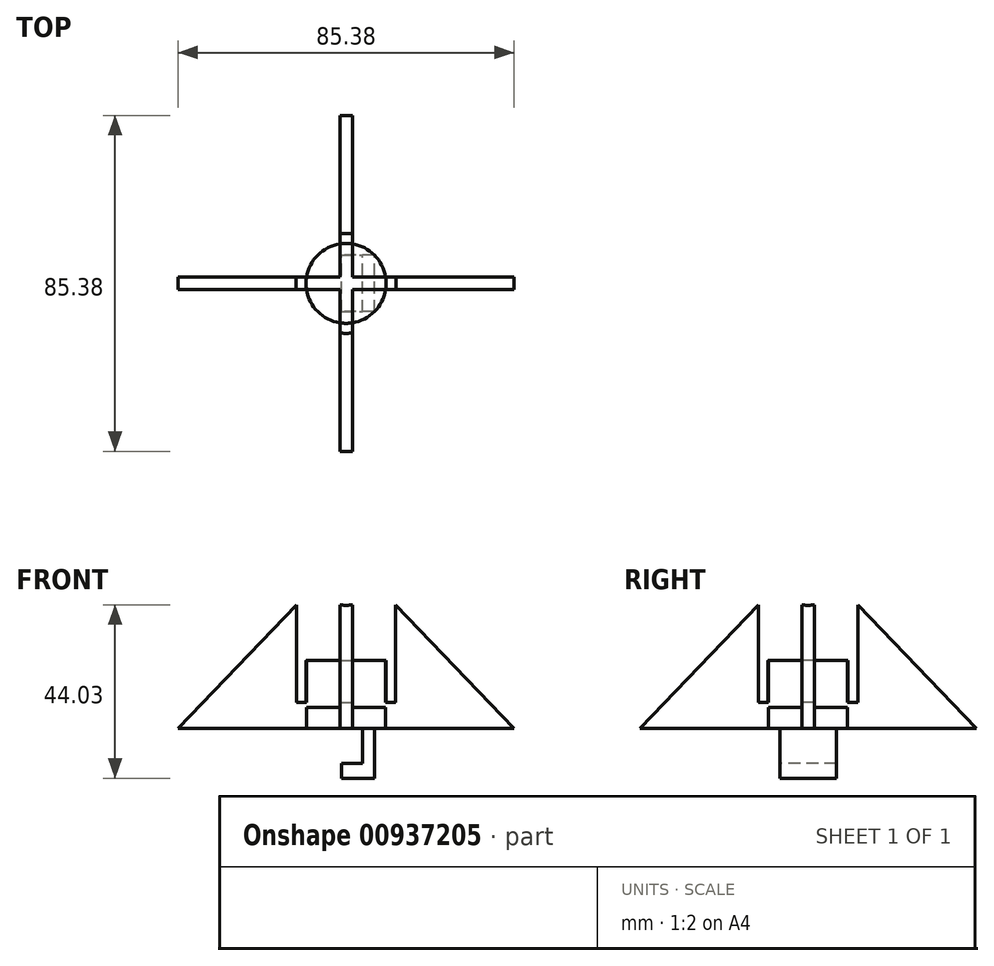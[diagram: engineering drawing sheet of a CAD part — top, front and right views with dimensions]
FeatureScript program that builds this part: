
annotation { "Feature Type Name" : "Feature", "Feature Type Description" : "" }
export const myFeature = defineFeature(function(context is Context, id is Id, definition is map)
    precondition{}
    {
        {
            var Q0;
            Q0=qCreatedBy(makeId("Top.planeOp"),FACE);
            var sketch = newSketch(context, id + "F0", { "sketchPlane" : qUnion([Q0])});
            skPoint(sketch, "E0", {"position": v(-50.8, 50.8) * mm});
            skLineSegment(sketch, "E1.bottom", {"start": v(-50.8, 50.8) * mm, "end": v(50.8, 50.8) * mm});
            skLineSegment(sketch, "E1.top", {"start": v(-50.8, -50.8) * mm, "end": v(50.8, -50.8) * mm});
            skLineSegment(sketch, "E1.left", {"start": v(-50.8, 50.8) * mm, "end": v(-50.8, -50.8) * mm});
            skLineSegment(sketch, "E1.right", {"start": v(50.8, 50.8) * mm, "end": v(50.8, -50.8) * mm});
            skPoint(sketch, "E1.middle", {"position": v(0, 0) * mm});
            skSolve(sketch);
        }
        {
            var Q0;
            Q0=makeQuery(id+"F0.imprint","IMPRINT",FACE,{"disambiguationData":[TD([[makeQuery(id+"F0.imprint","IMPRINT",EDGE,{"derivedFrom":sQuery(id+"F0.wireOp",EDGE,"E1.bottom")}),-1.0]])]});
            extrude(context, id + "F1", {"entities" : qUnion([Q0]), "depth" : 50.8 * mm, "offsetDistance" : 25.4 * mm});
        }
        {
            var Q0;
            Q0=makeQuery(id+"F1.opExtrude","CAP_FACE",FACE,{"disambiguationData":[OSD([sQuery(id+"F0.wireOp",EDGE,"E1.bottom"),sQuery(id+"F0.wireOp",EDGE,"E1.top"),sQuery(id+"F0.wireOp",EDGE,"E1.left"),sQuery(id+"F0.wireOp",EDGE,"E1.right")])],"isStart":false});
            var sketch = newSketch(context, id + "F2", { "sketchPlane" : qUnion([Q0])});
            skPoint(sketch, "E2.middle", {"position": v(0, 0) * mm});
            skLineSegment(sketch, "E3.bottom", {"start": v(-50.8, 50.8) * mm, "end": v(-1.59, 50.8) * mm});
            skLineSegment(sketch, "E3.top", {"start": v(-42.69, 1.59) * mm, "end": v(-1.59, 1.59) * mm});
            skLineSegment(sketch, "E3.left", {"start": v(-50.8, 50.8) * mm, "end": v(-50.8, 1.59) * mm});
            skLineSegment(sketch, "E3.right", {"start": v(-1.59, 42.69) * mm, "end": v(-1.59, 1.59) * mm});
            skLineSegment(sketch, "E4.bottom", {"start": v(1.59, 1.59) * mm, "end": v(42.69, 1.59) * mm});
            skLineSegment(sketch, "E4.top", {"start": v(1.59, 50.8) * mm, "end": v(50.8, 50.8) * mm});
            skLineSegment(sketch, "E4.left", {"start": v(1.59, 1.59) * mm, "end": v(1.59, 42.69) * mm});
            skLineSegment(sketch, "E4.right", {"start": v(50.8, 1.59) * mm, "end": v(50.8, 50.8) * mm});
            skLineSegment(sketch, "E5.bottom", {"start": v(1.59, -1.59) * mm, "end": v(42.69, -1.59) * mm});
            skLineSegment(sketch, "E5.top", {"start": v(1.59, -50.8) * mm, "end": v(50.8, -50.8) * mm});
            skLineSegment(sketch, "E5.left", {"start": v(1.59, -1.59) * mm, "end": v(1.59, -42.69) * mm});
            skLineSegment(sketch, "E5.right", {"start": v(50.8, -1.59) * mm, "end": v(50.8, -50.8) * mm});
            skLineSegment(sketch, "E6.bottom", {"start": v(-1.59, -1.59) * mm, "end": v(-42.69, -1.59) * mm});
            skLineSegment(sketch, "E6.top", {"start": v(-1.59, -50.8) * mm, "end": v(-50.8, -50.8) * mm});
            skLineSegment(sketch, "E6.left", {"start": v(-1.59, -1.59) * mm, "end": v(-1.59, -42.69) * mm});
            skLineSegment(sketch, "E6.right", {"start": v(-50.8, -1.59) * mm, "end": v(-50.8, -50.8) * mm});
            skLineSegment(sketch, "E7", {"start": v(-42.69, -1.59) * mm, "end": v(-42.69, 1.59) * mm});
            skLineSegment(sketch, "E8", {"start": v(-1.59, 42.69) * mm, "end": v(1.59, 42.69) * mm});
            skLineSegment(sketch, "E9", {"start": v(42.69, 1.59) * mm, "end": v(42.69, -1.59) * mm});
            skLineSegment(sketch, "E10", {"start": v(1.59, -42.69) * mm, "end": v(-1.59, -42.69) * mm});
            skLineSegment(sketch, "E11", {"start": v(-50.8, -1.59) * mm, "end": v(-50.8, 1.59) * mm});
            skLineSegment(sketch, "E12", {"start": v(-1.59, 50.8) * mm, "end": v(1.59, 50.8) * mm});
            skLineSegment(sketch, "E13", {"start": v(50.8, 1.59) * mm, "end": v(50.8, -1.59) * mm});
            skLineSegment(sketch, "E14", {"start": v(1.59, -50.8) * mm, "end": v(-1.59, -50.8) * mm});
            skLineSegment(sketch, "E15", {"start": v(0, -42.69) * mm, "end": v(0, -50.8) * mm, "construction": true});
            skLineSegment(sketch, "E16", {"start": v(50.8, 0) * mm, "end": v(42.69, 0) * mm, "construction": true});
            skLineSegment(sketch, "E17", {"start": v(0, 50.8) * mm, "end": v(0, 42.69) * mm, "construction": true});
            skLineSegment(sketch, "E18", {"start": v(-42.69, 0) * mm, "end": v(-50.8, 0) * mm, "construction": true});
            skSolve(sketch);
        }
        {
            var Q0;
            Q0=makeQuery(id+"F2.imprint","IMPRINT",FACE,{"disambiguationData":[TD([[makeQuery(id+"F2.imprint","IMPRINT",EDGE,{"derivedFrom":sQuery(id+"F2.wireOp",EDGE,"E3.bottom")}),-1.0]])]});
            extrude(context, id + "F3", {"entities" : qUnion([Q0]), "operationType" : NewBodyOperationType.REMOVE, "endBound" : BoundingType.THROUGH_ALL, "oppositeDirection" : true, "depth" : 25.4 * mm, "offsetDistance" : 25.4 * mm});
        }
        {
            var Q0;
            Q0=qCreatedBy(makeId("Front.planeOp"),FACE);
            var sketch = newSketch(context, id + "F4", { "sketchPlane" : qUnion([Q0])});
            skLineSegment(sketch, "E19", {"start": v(42.69, 0) * mm, "end": v(42.69, 50.8) * mm});
            skLineSegment(sketch, "E20", {"start": v(42.69, 50.8) * mm, "end": v(-42.69, 50.8) * mm});
            skLineSegment(sketch, "E21", {"start": v(-42.69, 50.8) * mm, "end": v(-42.69, 0) * mm});
            skPoint(sketch, "E22", {"position": v(0, 44.45) * mm});
            skPoint(sketch, "E22.positionSnap0", {"position": v(0, 50.8) * mm});
            skLineSegment(sketch, "E23", {"start": v(-42.69, 0) * mm, "end": v(0, 44.45) * mm});
            skLineSegment(sketch, "E24", {"start": v(0, 44.45) * mm, "end": v(42.69, 0) * mm});
            skSolve(sketch);
        }
        {
            var Q0;
            Q0 = qSketchRegion(id + "F4", true);
            extrude(context, id + "F5", {"entities" : qUnion([Q0]), "operationType" : NewBodyOperationType.REMOVE, "endBound" : BoundingType.THROUGH_ALL, "oppositeDirection" : true, "depth" : 25.4 * mm, "offsetDistance" : 25.4 * mm, "hasSecondDirection" : true, "secondDirectionBound" : SecondDirectionBoundingType.THROUGH_ALL, "secondDirectionOppositeDirection" : false, "secondDirectionDepth" : 25.4 * mm});
        }
        {
            var Q0;
            Q0=qCreatedBy(makeId("Right.planeOp"),FACE);
            var sketch = newSketch(context, id + "F6", { "sketchPlane" : qUnion([Q0])});
            skLineSegment(sketch, "E25", {"start": v(-42.69, 0) * mm, "end": v(-42.69, 50.8) * mm});
            skLineSegment(sketch, "E26", {"start": v(-42.69, 50.8) * mm, "end": v(42.69, 50.8) * mm});
            skLineSegment(sketch, "E27", {"start": v(42.69, 50.8) * mm, "end": v(42.69, 0) * mm});
            skPoint(sketch, "E28", {"position": v(0, 50.8) * mm});
            skPoint(sketch, "E29", {"position": v(0, 44.45) * mm});
            skLineSegment(sketch, "E30", {"start": v(-42.69, 0) * mm, "end": v(0, 44.45) * mm});
            skLineSegment(sketch, "E31", {"start": v(0, 44.45) * mm, "end": v(42.69, 0) * mm});
            skSolve(sketch);
        }
        {
            var Q0;
            Q0 = qSketchRegion(id + "F6", true);
            extrude(context, id + "F7", {"entities" : qUnion([Q0]), "operationType" : NewBodyOperationType.REMOVE, "endBound" : BoundingType.THROUGH_ALL, "oppositeDirection" : true, "depth" : 25.4 * mm, "offsetDistance" : 25.4 * mm, "hasSecondDirection" : true, "secondDirectionBound" : SecondDirectionBoundingType.THROUGH_ALL, "secondDirectionOppositeDirection" : false, "secondDirectionDepth" : 25.4 * mm});
        }
        {
            var Q0;
            Q0=qCreatedBy(makeId("Front.planeOp"),FACE);
            var sketch = newSketch(context, id + "F8", { "sketchPlane" : qUnion([Q0])});
            skLineSegment(sketch, "E32", {"start": v(-9.6, 42.58) * mm, "end": v(15.04, 42.58) * mm});
            skLineSegment(sketch, "E33", {"start": v(15.04, 42.58) * mm, "end": v(0, 64.32) * mm});
            skLineSegment(sketch, "E34", {"start": v(0, 64.32) * mm, "end": v(-9.6, 42.58) * mm});
            skSolve(sketch);
        }
        {
            var Q0;
            Q0 = qSketchRegion(id + "F8", true);
            extrude(context, id + "F9", {"entities" : qUnion([Q0]), "operationType" : NewBodyOperationType.REMOVE, "oppositeDirection" : true, "depth" : 25.4 * mm, "offsetDistance" : 25.4 * mm, "hasSecondDirection" : true, "secondDirectionOppositeDirection" : false, "secondDirectionDepth" : 25.4 * mm});
        }
        {
            var Q0;
            Q0=makeQuery(id+"F9.boolean.opBoolean","COPY",FACE,{"derivedFrom":makeQuery(id+"F9.opExtrude","SWEPT_FACE",FACE,{"disambiguationData":[OSD([sQuery(id+"F8.wireOp",EDGE,"E32")])]})});
            var sketch = newSketch(context, id + "F10", { "sketchPlane" : qUnion([Q0])});
            skCircle(sketch, "E35", {"center": v(0, 0) * mm, "radius": 12.7 * mm});
            skCircle(sketch, "E36", {"center": v(0, 0) * mm, "radius": 10.16 * mm});
            skSolve(sketch);
        }
        {
            var Q0;
            Q0=makeQuery(id+"F10.imprint","IMPRINT",FACE,{"disambiguationData":[TD([[makeQuery(id+"F10.imprint","IMPRINT",EDGE,{"derivedFrom":sQuery(id+"F10.wireOp",EDGE,"E35")}),1.0]])]});
            extrude(context, id + "F11", {"entities" : qUnion([Q0]), "operationType" : NewBodyOperationType.REMOVE, "oppositeDirection" : true, "depth" : 36.07 * mm, "offsetDistance" : 25.4 * mm});
        }
        {
            var Q0;
            Q0=makeQuery(id+"F9.boolean.opBoolean","COPY",FACE,{"derivedFrom":makeQuery(id+"F9.opExtrude","SWEPT_FACE",FACE,{"disambiguationData":[OSD([sQuery(id+"F8.wireOp",EDGE,"E32")])]})});
            var sketch = newSketch(context, id + "F12", { "sketchPlane" : qUnion([Q0])});
            skCircle(sketch, "E37", {"center": v(0, 0) * mm, "radius": 10.16 * mm});
            skSolve(sketch);
        }
        {
            var Q0;
            Q0 = qSketchRegion(id + "F12", true);
            extrude(context, id + "F13", {"entities" : qUnion([Q0]), "operationType" : NewBodyOperationType.REMOVE, "oppositeDirection" : true, "depth" : 25.4 * mm, "offsetDistance" : 25.4 * mm});
        }
        {
            var Q0;
            Q0=qCreatedBy(makeId("Top.planeOp"),FACE);
            var sketch = newSketch(context, id + "F14", { "sketchPlane" : qUnion([Q0])});
            skCircle(sketch, "E38", {"center": v(0, 0) * mm, "radius": 10.16 * mm});
            skSolve(sketch);
        }
        {
            var Q0;
            Q0 = qSketchRegion(id + "F14", true);
            extrude(context, id + "F15", {"entities" : qUnion([Q0]), "operationType" : NewBodyOperationType.ADD, "depth" : 5.33 * mm, "offsetDistance" : 25.4 * mm});
        }
        {
            var Q0;
            Q0=makeQuery(id+"F15.boolean.opBoolean","MERGE",FACE,{"derivedFrom":[makeQuery(id+"F1.opExtrude","CAP_FACE",FACE,{"disambiguationData":[OSD([sQuery(id+"F0.wireOp",EDGE,"E1.bottom"),sQuery(id+"F0.wireOp",EDGE,"E1.top"),sQuery(id+"F0.wireOp",EDGE,"E1.left"),sQuery(id+"F0.wireOp",EDGE,"E1.right")])],"isStart":true}),makeQuery(id+"F15.opExtrude","CAP_FACE",FACE,{"disambiguationData":[OSD([sQuery(id+"F14.wireOp",EDGE,"E38")])],"isStart":true})]});
            var sketch = newSketch(context, id + "F16", { "sketchPlane" : qUnion([Q0])});
            skPoint(sketch, "E39.oppositeSnap0", {"position": v(7.18, -7.18) * mm});
            skLineSegment(sketch, "E39.bottom", {"start": v(7.18, 7.18) * mm, "end": v(4.14, 7.18) * mm});
            skLineSegment(sketch, "E39.top", {"start": v(7.18, -7.18) * mm, "end": v(4.14, -7.18) * mm});
            skLineSegment(sketch, "E39.left", {"start": v(7.18, 7.18) * mm, "end": v(7.18, -7.18) * mm});
            skLineSegment(sketch, "E39.right", {"start": v(4.14, 7.18) * mm, "end": v(4.14, -7.18) * mm});
            skSolve(sketch);
        }
        {
            var Q0;
            Q0 = qSketchRegion(id + "F16", true);
            extrude(context, id + "F17", {"entities" : qUnion([Q0]), "operationType" : NewBodyOperationType.ADD, "depth" : 12.7 * mm, "offsetDistance" : 25.4 * mm});
        }
        {
            var Q0;
            Q0=makeQuery(id+"F17.opExtrude","SWEPT_FACE",FACE,{"disambiguationData":[OSD([sQuery(id+"F16.wireOp",EDGE,"E39.right")])]});
            var sketch = newSketch(context, id + "F18", { "sketchPlane" : qUnion([Q0])});
            skLineSegment(sketch, "E40.bottom", {"start": v(-7.18, -12.7) * mm, "end": v(7.18, -12.7) * mm});
            skLineSegment(sketch, "E40.top", {"start": v(-7.18, -8.9) * mm, "end": v(7.18, -8.9) * mm});
            skLineSegment(sketch, "E40.left", {"start": v(-7.18, -12.7) * mm, "end": v(-7.18, -8.9) * mm});
            skLineSegment(sketch, "E40.right", {"start": v(7.18, -12.7) * mm, "end": v(7.18, -8.9) * mm});
            skSolve(sketch);
        }
        {
            var Q0;
            Q0=makeQuery(id+"F18.imprint","IMPRINT",FACE,{"disambiguationData":[TD([[makeQuery(id+"F18.imprint","IMPRINT",EDGE,{"derivedFrom":sQuery(id+"F18.wireOp",EDGE,"E40.bottom")}),-1.0]])]});
            extrude(context, id + "F19", {"entities" : qUnion([Q0]), "operationType" : NewBodyOperationType.ADD, "depth" : 5.33 * mm, "offsetDistance" : 25.4 * mm});
        }
    });
